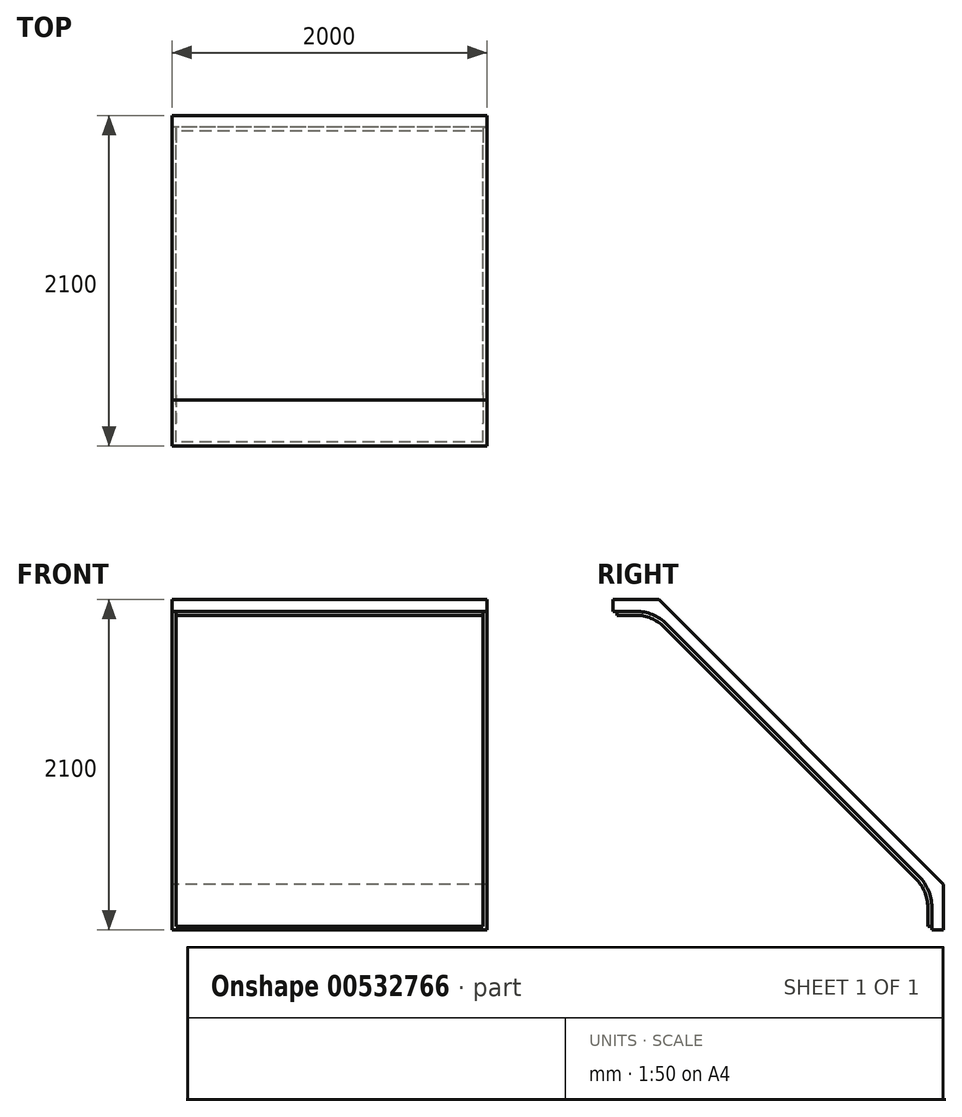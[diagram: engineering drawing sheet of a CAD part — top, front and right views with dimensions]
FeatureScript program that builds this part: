
annotation { "Feature Type Name" : "Feature", "Feature Type Description" : "" }
export const myFeature = defineFeature(function(context is Context, id is Id, definition is map)
    precondition{}
    {
        {
            var Q0;
            Q0=qCreatedBy(makeId("Right.planeOp"),FACE);
            var sketch = newSketch(context, id + "F0", { "sketchPlane" : qUnion([Q0])});
            skLineSegment(sketch, "E0.bottom", {"start": v(0, 0) * mm, "end": v(-2000, 0) * mm, "construction": true});
            skLineSegment(sketch, "E0.top", {"start": v(0, 2000) * mm, "end": v(-2000, 2000) * mm, "construction": true});
            skLineSegment(sketch, "E0.left", {"start": v(0, 0) * mm, "end": v(0, 2000) * mm, "construction": true});
            skLineSegment(sketch, "E0.right", {"start": v(-2000, 0) * mm, "end": v(-2000, 2000) * mm, "construction": true});
            skLineSegment(sketch, "E1", {"start": v(-2000, 2000) * mm, "end": v(-1750, 2000) * mm});
            skLineSegment(sketch, "E2", {"start": v(-1750, 2000) * mm, "end": v(0, 250) * mm});
            skLineSegment(sketch, "E3", {"start": v(0, 250) * mm, "end": v(0, 0) * mm});
            skLineSegment(sketch, "E4.0", {"start": v(100, 291.42) * mm, "end": v(100, 0) * mm});
            skLineSegment(sketch, "E4.1", {"start": v(-1708.58, 2100) * mm, "end": v(100, 291.42) * mm});
            skLineSegment(sketch, "E4.2", {"start": v(-2000, 2100) * mm, "end": v(-1708.58, 2100) * mm});
            skLineSegment(sketch, "E5", {"start": v(-2000, 2100) * mm, "end": v(-2000, 2000) * mm});
            skLineSegment(sketch, "E6", {"start": v(100, 0) * mm, "end": v(0, 0) * mm});
            skSolve(sketch);
        }
        {
            var Q0;
            Q0=makeQuery(id+"F0.imprint","IMPRINT",FACE,{"disambiguationData":[TD([[makeQuery(id+"F0.imprint","IMPRINT",EDGE,{"derivedFrom":sQuery(id+"F0.wireOp",EDGE,"E1")}),1.0]])]});
            extrude(context, id + "F1", {"entities" : qUnion([Q0]), "depth" : 2000 * mm, "offsetDistance" : 25 * mm});
        }
        {
            var Q0;
            Q0=makeQuery(id+"F1.opExtrude","SWEPT_EDGE",EDGE,{"disambiguationData":[OSD([sQuery(id+"F0.wireOp",EDGE,"E1"),sQuery(id+"F0.wireOp",EDGE,"E2")])]});
            var Q1;
            Q1=makeQuery(id+"F1.opExtrude","SWEPT_EDGE",EDGE,{"disambiguationData":[OSD([sQuery(id+"F0.wireOp",EDGE,"E2"),sQuery(id+"F0.wireOp",EDGE,"E3")])]});
            fillet(context, id + "F2", {"entities" : qUnion([Q0, Q1]), "radius" : 250 * mm, "tangentPropagation" : true, "allowEdgeOverflow" : false});
        }
        {
            var Q0;
            Q0=makeQuery(id+"F1.opExtrude","CAP_FACE",FACE,{"disambiguationData":[OSD([sQuery(id+"F0.wireOp",EDGE,"E1"),sQuery(id+"F0.wireOp",EDGE,"E2"),sQuery(id+"F0.wireOp",EDGE,"E3"),sQuery(id+"F0.wireOp",EDGE,"E4.0"),sQuery(id+"F0.wireOp",EDGE,"E4.1"),sQuery(id+"F0.wireOp",EDGE,"E4.2"),sQuery(id+"F0.wireOp",EDGE,"E5"),sQuery(id+"F0.wireOp",EDGE,"E6")])],"isStart":true});
            var sketch = newSketch(context, id + "F3", { "sketchPlane" : qUnion([Q0])});
            skLineSegment(sketch, "E7.0", {"start": v(-25, 146.45) * mm, "end": v(-25, 0) * mm});
            skLineSegment(sketch, "E7.1", {"start": v(2000, 2025) * mm, "end": v(1853.55, 2025) * mm});
            skArc(sketch, "E7.2", {"start": v(1659.1, 1944.45) * mm, "mid": v(1748.32, 2004.07) * mm, "end": v(1853.55, 2025) * mm});
            skLineSegment(sketch, "E7.3", {"start": v(1659.1, 1944.45) * mm, "end": v(55.55, 340.9) * mm});
            skArc(sketch, "E7.4", {"start": v(-25, 146.45) * mm, "mid": v(-4.07, 251.68) * mm, "end": v(55.55, 340.9) * mm});
            skSolve(sketch);
        }
        {
            var Q0;
            {var subQ7=sQuery(id+"F3.wireOp",EDGE,"E7.0");Q0=makeQuery(id+"F3.imprint","IMPRINT",FACE,{"disambiguationData":[TD([[makeQuery(id+"F3.imprint","IMPRINT",EDGE,{"derivedFrom":subQ7}),1.0]])]});}
            extrude(context, id + "F4", {"entities" : qUnion([Q0]), "operationType" : NewBodyOperationType.REMOVE, "oppositeDirection" : true, "depth" : 25 * mm, "offsetDistance" : 25 * mm});
        }
        {
            var Q0;
            Q0=makeQuery(id+"F1.opExtrude","CAP_FACE",FACE,{"disambiguationData":[OSD([sQuery(id+"F0.wireOp",EDGE,"E1"),sQuery(id+"F0.wireOp",EDGE,"E2"),sQuery(id+"F0.wireOp",EDGE,"E3"),sQuery(id+"F0.wireOp",EDGE,"E4.0"),sQuery(id+"F0.wireOp",EDGE,"E4.1"),sQuery(id+"F0.wireOp",EDGE,"E4.2"),sQuery(id+"F0.wireOp",EDGE,"E5"),sQuery(id+"F0.wireOp",EDGE,"E6")])],"isStart":false});
            var sketch = newSketch(context, id + "F5", { "sketchPlane" : qUnion([Q0])});
            skLineSegment(sketch, "E8.0", {"start": v(25, 146.45) * mm, "end": v(25, 0) * mm});
            skLineSegment(sketch, "E8.1", {"start": v(-2000, 2025) * mm, "end": v(-1853.55, 2025) * mm});
            skArc(sketch, "E8.2", {"start": v(-1853.55, 2025) * mm, "mid": v(-1748.32, 2004.07) * mm, "end": v(-1659.1, 1944.45) * mm});
            skLineSegment(sketch, "E8.3", {"start": v(-1659.1, 1944.45) * mm, "end": v(-55.55, 340.9) * mm});
            skArc(sketch, "E8.4", {"start": v(-55.55, 340.9) * mm, "mid": v(4.07, 251.68) * mm, "end": v(25, 146.45) * mm});
            skSolve(sketch);
        }
        {
            var Q0;
            {var subQ7=sQuery(id+"F5.wireOp",EDGE,"E8.0");Q0=makeQuery(id+"F5.imprint","IMPRINT",FACE,{"disambiguationData":[TD([[makeQuery(id+"F5.imprint","IMPRINT",EDGE,{"derivedFrom":subQ7}),-1.0]])]});}
            extrude(context, id + "F6", {"entities" : qUnion([Q0]), "operationType" : NewBodyOperationType.REMOVE, "oppositeDirection" : true, "depth" : 25 * mm, "offsetDistance" : 25 * mm});
        }
        {
            var Q0;
            Q0=makeQuery(id+"F1.opExtrude","SWEPT_FACE",FACE,{"disambiguationData":[OSD([sQuery(id+"F0.wireOp",EDGE,"E5")])]});
            var sketch = newSketch(context, id + "F7", { "sketchPlane" : qUnion([Q0])});
            skLineSegment(sketch, "E9.0", {"start": v(1975, 2025) * mm, "end": v(25, 2025) * mm});
            skSolve(sketch);
        }
        {
            var Q0;
            Q0=makeQuery(id+"F7.imprint","IMPRINT",FACE,{"disambiguationData":[TD([[makeQuery(id+"F7.imprint","IMPRINT",EDGE,{"derivedFrom":sQuery(id+"F7.wireOp",EDGE,"E9.0")}),1.0]])]});
            extrude(context, id + "F8", {"entities" : qUnion([Q0]), "operationType" : NewBodyOperationType.REMOVE, "oppositeDirection" : true, "depth" : 25 * mm, "offsetDistance" : 25 * mm});
        }
        {
            var Q0;
            Q0=makeQuery(id+"F1.opExtrude","SWEPT_FACE",FACE,{"disambiguationData":[OSD([sQuery(id+"F0.wireOp",EDGE,"E6")])]});
            var sketch = newSketch(context, id + "F9", { "sketchPlane" : qUnion([Q0])});
            skLineSegment(sketch, "E10.0", {"start": v(1975, -25) * mm, "end": v(25, -25) * mm});
            skSolve(sketch);
        }
        {
            var Q0;
            Q0=makeQuery(id+"F9.imprint","IMPRINT",FACE,{"disambiguationData":[TD([[makeQuery(id+"F9.imprint","IMPRINT",EDGE,{"derivedFrom":sQuery(id+"F9.wireOp",EDGE,"E10.0")}),-1.0]])]});
            extrude(context, id + "F10", {"entities" : qUnion([Q0]), "operationType" : NewBodyOperationType.REMOVE, "oppositeDirection" : true, "depth" : 25 * mm, "offsetDistance" : 25 * mm});
        }
    });
